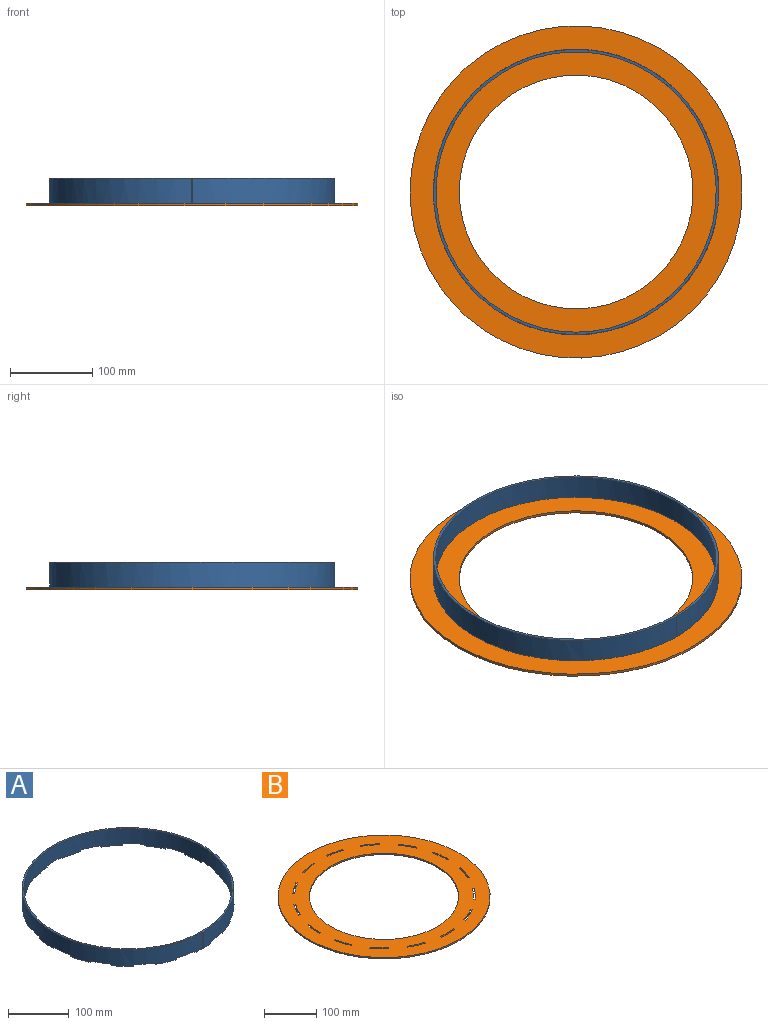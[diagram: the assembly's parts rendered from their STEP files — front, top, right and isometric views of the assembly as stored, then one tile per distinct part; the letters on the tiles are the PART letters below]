
ASSEMBLY  parts=2 mates=1
PART A: 66 faces, bbox 347.8x347.8x33 mm
  f0: plane 3x2.85mm, normal (-0.95,-0.31,0), area 9mm2, adj f1,f63,f64,f65
  f1: plane 34.14x17.39mm, normal (0,0,-1), area 108.3mm2, adj f0,f2,f64,f65
  f2: plane 3x2.6mm, normal (0.87,0.5,0), area 9mm2, adj f1,f3,f64,f65
  f3: plane 30.91x23.6mm, normal (0,0,-1), area 108.3mm2, adj f2,f4,f64,f65
  f4: plane 3x2.23mm, normal (-0.74,-0.67,0), area 9mm2, adj f3,f5,f64,f65
  f5: plane 28.78x26.33mm, normal (0,0,-1), area 108.3mm2, adj f4,f6,f64,f65
  f6: plane 3x2.43mm, normal (0.59,0.81,0), area 9mm2, adj f5,f7,f64,f65
  f7: plane 32.7x20.6mm, normal (0,0,-1), area 108.3mm2, adj f6,f8,f64,f65
  f8: plane 3x2.74mm, normal (-0.41,-0.91,0), area 9mm2, adj f7,f9,f64,f65
  f9: plane 35.2x13.98mm, normal (0,0,-1), area 108.3mm2, adj f8,f10,f64,f65
  f10: plane 3x2.93mm, normal (0.21,0.98,0), area 9mm2, adj f9,f11,f64,f65
  f11: plane 36.16x6.73mm, normal (0,0,-1), area 108.3mm2, adj f10,f12,f64,f65
  f12: plane 3x3mm, normal (0,-1,0), area 9mm2, adj f11,f13,f64,f65
  f13: plane 36.16x6.73mm, normal (0,0,-1), area 108.3mm2, adj f12,f14,f64,f65
  f14: plane 3x2.93mm, normal (-0.21,0.98,0), area 9mm2, adj f13,f15,f64,f65
  f15: plane 35.2x13.98mm, normal (0,0,-1), area 108.3mm2, adj f14,f16,f64,f65
  f16: plane 3x2.74mm, normal (0.41,-0.91,0), area 9mm2, adj f15,f17,f64,f65
  f17: plane 32.7x20.6mm, normal (0,0,-1), area 108.3mm2, adj f16,f18,f64,f65
  f18: plane 3x2.43mm, normal (-0.59,0.81,0), area 9mm2, adj f17,f19,f64,f65
  f19: plane 28.78x26.33mm, normal (0,0,-1), area 108.3mm2, adj f18,f20,f64,f65
  f20: plane 3x2.23mm, normal (0.74,-0.67,0), area 9mm2, adj f19,f21,f64,f65
  f21: plane 30.91x23.6mm, normal (0,0,-1), area 108.3mm2, adj f20,f22,f64,f65
  f22: plane 3x2.6mm, normal (-0.87,0.5,0), area 9mm2, adj f21,f23,f64,f65
  f23: plane 34.14x17.39mm, normal (0,0,-1), area 108.3mm2, adj f22,f24,f64,f65
  f24: plane 3x2.85mm, normal (0.95,-0.31,0), area 9mm2, adj f23,f25,f64,f65
  f25: plane 35.87x10.41mm, normal (0,0,-1), area 108.3mm2, adj f24,f26,f64,f65
  f26: plane 3x2.98mm, normal (-0.99,0.1,0), area 9mm2, adj f25,f27,f64,f65
  f27: plane 18.08x3.94mm, normal (0,0,-1), area 53.9mm2, adj f26,f28,f64,f65
  f28: plane 33x3mm, normal (1,0,0), area 99mm2, adj f27,f29,f64,f65
  f29: plane 347.8x347.8mm, normal (0,0,1), area 3249.1mm2, adj f28,f30,f64,f65
  f30: plane 33x3mm, normal (-1,0,0), area 99mm2, adj f29,f31,f64,f65
  f31: plane 18.08x3.94mm, normal (0,0,-1), area 53.9mm2, adj f30,f32,f64,f65
  f32: plane 3x2.98mm, normal (0.99,0.1,0), area 9mm2, adj f31,f33,f64,f65
  f33: plane 35.87x10.41mm, normal (0,0,-1), area 108.3mm2, adj f32,f34,f64,f65
  f34: plane 3x2.85mm, normal (-0.95,-0.31,0), area 9mm2, adj f33,f35,f64,f65
  f35: plane 34.14x17.39mm, normal (0,0,-1), area 108.3mm2, adj f34,f36,f64,f65
  f36: plane 3x2.6mm, normal (0.87,0.5,0), area 9mm2, adj f35,f37,f64,f65
  f37: plane 30.91x23.6mm, normal (0,0,-1), area 108.3mm2, adj f36,f38,f64,f65
  f38: plane 3x2.23mm, normal (-0.74,-0.67,0), area 9mm2, adj f37,f39,f64,f65
  f39: plane 28.78x26.33mm, normal (0,0,-1), area 108.3mm2, adj f38,f40,f64,f65
  f40: plane 3x2.43mm, normal (0.59,0.81,0), area 9mm2, adj f39,f41,f64,f65
  f41: plane 32.7x20.6mm, normal (0,0,-1), area 108.3mm2, adj f40,f42,f64,f65
  f42: plane 3x2.74mm, normal (-0.41,-0.91,0), area 9mm2, adj f41,f43,f64,f65
  f43: plane 35.2x13.98mm, normal (0,0,-1), area 108.3mm2, adj f42,f44,f64,f65
  f44: plane 3x2.93mm, normal (0.21,0.98,0), area 9mm2, adj f43,f45,f64,f65
  f45: plane 36.16x6.73mm, normal (0,0,-1), area 108.3mm2, adj f44,f46,f64,f65
  f46: plane 3x3mm, normal (0,-1,0), area 9mm2, adj f45,f47,f64,f65
  f47: plane 36.16x6.73mm, normal (0,0,-1), area 108.3mm2, adj f46,f48,f64,f65
  f48: plane 3x2.93mm, normal (-0.21,0.98,0), area 9mm2, adj f47,f49,f64,f65
  f49: plane 35.2x13.98mm, normal (0,0,-1), area 108.3mm2, adj f48,f50,f64,f65
  f50: plane 3x2.74mm, normal (0.41,-0.91,0), area 9mm2, adj f49,f51,f64,f65
  f51: plane 32.7x20.6mm, normal (0,0,-1), area 108.3mm2, adj f50,f52,f64,f65
  f52: plane 3x2.43mm, normal (-0.59,0.81,0), area 9mm2, adj f51,f53,f64,f65
  f53: plane 28.78x26.33mm, normal (0,0,-1), area 108.3mm2, adj f52,f54,f64,f65
  f54: plane 3x2.23mm, normal (0.74,-0.67,0), area 9mm2, adj f53,f55,f64,f65
  f55: plane 30.91x23.6mm, normal (0,0,-1), area 108.3mm2, adj f54,f56,f64,f65
  f56: plane 3x2.6mm, normal (-0.87,0.5,0), area 9mm2, adj f55,f57,f64,f65
  f57: plane 34.14x17.39mm, normal (0,0,-1), area 108.3mm2, adj f56,f58,f64,f65
  f58: plane 3x2.85mm, normal (0.95,-0.31,0), area 9mm2, adj f57,f59,f64,f65
  f59: plane 35.87x10.41mm, normal (0,0,-1), area 108.3mm2, adj f58,f60,f64,f65
  f60: plane 3x2.98mm, normal (-0.99,0.1,0), area 9mm2, adj f59,f61,f64,f65
  f61: plane 36.36x3.94mm, normal (0,0,-1), area 108.3mm2, adj f60,f62,f64,f65
  f62: plane 3x2.98mm, normal (0.99,0.1,0), area 9mm2, adj f61,f63,f64,f65
  f63: plane 35.87x10.41mm, normal (0,0,-1), area 108.3mm2, adj f0,f62,f64,f65
  f64: cylinder r=173.9mm len=347.8mm, axis (0,0,1), area 34411.6mm2, adj f0,f1,f2,f3,f4,f5,f6,f7
  f65: cylinder r=170.9mm len=341.8mm, axis (0,0,1), area 33818mm2, adj f0,f1,f2,f3,f4,f5,f6,f7
PART B: 64 faces, bbox 405x405x3 mm
  f0: plane 3.04x3mm, normal (-0.95,0.31,0), area 9.6mm2, adj f1,f46,f62,f63
  f1: cylinder r=170.9mm len=34.95mm, axis (0,0,-1), area 107.4mm2, adj f0,f2,f62,f63
  f2: plane 3.18x3mm, normal (0.99,-0.1,0), area 9.6mm2, adj f1,f46,f62,f63
  f3: cylinder r=170.9mm len=28.9mm, axis (0,0,-1), area 107.4mm2, adj f4,f47,f62,f63
  f4: plane 3x2.77mm, normal (0.87,-0.5,0), area 9.6mm2, adj f3,f5,f62,f63
  f5: cylinder r=174.1mm len=29.45mm, axis (0,0,-1), area 109.4mm2, adj f4,f47,f62,f63
  f6: cylinder r=170.9mm len=30.94mm, axis (0,0,-1), area 107.4mm2, adj f7,f48,f62,f63
  f7: plane 3x2.59mm, normal (0.59,-0.81,0), area 9.6mm2, adj f6,f8,f62,f63
  f8: cylinder r=174.1mm len=31.52mm, axis (0,0,-1), area 109.4mm2, adj f7,f48,f62,f63
  f9: cylinder r=170.9mm len=35.53mm, axis (0,0,-1), area 107.4mm2, adj f10,f49,f62,f63
  f10: plane 3.13x3mm, normal (0.21,-0.98,0), area 9.6mm2, adj f9,f11,f62,f63
  f11: cylinder r=174.1mm len=36.2mm, axis (0,0,-1), area 109.4mm2, adj f10,f49,f62,f63
  f12: cylinder r=170.9mm len=33.98mm, axis (0,0,-1), area 107.4mm2, adj f13,f50,f62,f63
  f13: plane 3.13x3mm, normal (-0.21,-0.98,0), area 9.6mm2, adj f12,f14,f62,f63
  f14: cylinder r=174.1mm len=34.62mm, axis (0,0,-1), area 109.4mm2, adj f13,f50,f62,f63
  f15: cylinder r=170.9mm len=26.55mm, axis (0,0,-1), area 107.4mm2, adj f16,f51,f62,f63
  f16: plane 3x2.59mm, normal (-0.59,-0.81,0), area 9.6mm2, adj f15,f17,f62,f63
  f17: cylinder r=174.1mm len=27.05mm, axis (0,0,-1), area 109.4mm2, adj f16,f51,f62,f63
  f18: cylinder r=170.9mm len=32.64mm, axis (0,0,-1), area 107.4mm2, adj f19,f52,f62,f63
  f19: plane 3x2.77mm, normal (-0.87,-0.5,0), area 9.6mm2, adj f18,f20,f62,f63
  f20: cylinder r=174.1mm len=33.25mm, axis (0,0,-1), area 109.4mm2, adj f19,f52,f62,f63
  f21: cylinder r=170.9mm len=35.73mm, axis (0,0,-1), area 107.4mm2, adj f22,f53,f62,f63
  f22: plane 3.18x3mm, normal (-0.99,-0.1,0), area 9.6mm2, adj f21,f23,f62,f63
  f23: cylinder r=174.1mm len=36.4mm, axis (0,0,-1), area 109.4mm2, adj f22,f53,f62,f63
  f24: cylinder r=170.9mm len=32.64mm, axis (0,0,-1), area 107.4mm2, adj f25,f54,f62,f63
  f25: plane 3.04x3mm, normal (-0.95,0.31,0), area 9.6mm2, adj f24,f26,f62,f63
  f26: cylinder r=174.1mm len=33.25mm, axis (0,0,-1), area 109.4mm2, adj f25,f54,f62,f63
  f27: cylinder r=170.9mm len=26.55mm, axis (0,0,-1), area 107.4mm2, adj f28,f55,f62,f63
  f28: plane 3x2.38mm, normal (-0.74,0.67,0), area 9.6mm2, adj f27,f29,f62,f63
  f29: cylinder r=174.1mm len=27.05mm, axis (0,0,-1), area 109.4mm2, adj f28,f55,f62,f63
  f30: cylinder r=170.9mm len=33.98mm, axis (0,0,-1), area 107.4mm2, adj f31,f56,f62,f63
  f31: plane 3x2.92mm, normal (-0.41,0.91,0), area 9.6mm2, adj f30,f32,f62,f63
  f32: cylinder r=174.1mm len=34.62mm, axis (0,0,-1), area 109.4mm2, adj f31,f56,f62,f63
  f33: cylinder r=170.9mm len=35.53mm, axis (0,0,-1), area 107.4mm2, adj f34,f57,f62,f63
  f34: plane 3.2x3mm, normal (0,1,0), area 9.6mm2, adj f33,f35,f62,f63
  f35: cylinder r=174.1mm len=36.2mm, axis (0,0,-1), area 109.4mm2, adj f34,f57,f62,f63
  f36: cylinder r=170.9mm len=30.94mm, axis (0,0,-1), area 107.4mm2, adj f37,f58,f62,f63
  f37: plane 3x2.92mm, normal (0.41,0.91,0), area 9.6mm2, adj f36,f38,f62,f63
  f38: cylinder r=174.1mm len=31.52mm, axis (0,0,-1), area 109.4mm2, adj f37,f58,f62,f63
  f39: cylinder r=170.9mm len=28.9mm, axis (0,0,-1), area 107.4mm2, adj f40,f59,f62,f63
  f40: plane 3x2.38mm, normal (0.74,0.67,0), area 9.6mm2, adj f39,f41,f62,f63
  f41: cylinder r=174.1mm len=29.45mm, axis (0,0,-1), area 109.4mm2, adj f40,f59,f62,f63
  f42: cylinder r=170.9mm len=34.95mm, axis (0,0,-1), area 107.4mm2, adj f43,f60,f62,f63
  f43: plane 3.04x3mm, normal (0.95,0.31,0), area 9.6mm2, adj f42,f44,f62,f63
  f44: cylinder r=174.1mm len=35.6mm, axis (0,0,-1), area 109.4mm2, adj f43,f60,f62,f63
  f45: cylinder r=142.5mm len=285mm, axis (0,0,-1), area 2686.1mm2, adj f62,f63
  f46: cylinder r=174.1mm len=35.6mm, axis (0,0,-1), area 109.4mm2, adj f0,f2,f62,f63
  f47: plane 3x2.38mm, normal (-0.74,0.67,0), area 9.6mm2, adj f3,f5,f62,f63
  f48: plane 3x2.92mm, normal (-0.41,0.91,0), area 9.6mm2, adj f6,f8,f62,f63
  f49: plane 3.2x3mm, normal (0,1,0), area 9.6mm2, adj f9,f11,f62,f63
  f50: plane 3x2.92mm, normal (0.41,0.91,0), area 9.6mm2, adj f12,f14,f62,f63
  f51: plane 3x2.38mm, normal (0.74,0.67,0), area 9.6mm2, adj f15,f17,f62,f63
  f52: plane 3.04x3mm, normal (0.95,0.31,0), area 9.6mm2, adj f18,f20,f62,f63
  f53: plane 3.18x3mm, normal (0.99,-0.1,0), area 9.6mm2, adj f21,f23,f62,f63
  f54: plane 3x2.77mm, normal (0.87,-0.5,0), area 9.6mm2, adj f24,f26,f62,f63
  f55: plane 3x2.59mm, normal (0.59,-0.81,0), area 9.6mm2, adj f27,f29,f62,f63
  f56: plane 3.13x3mm, normal (0.21,-0.98,0), area 9.6mm2, adj f30,f32,f62,f63
  f57: plane 3.13x3mm, normal (-0.21,-0.98,0), area 9.6mm2, adj f33,f35,f62,f63
  f58: plane 3x2.59mm, normal (-0.59,-0.81,0), area 9.6mm2, adj f36,f38,f62,f63
  f59: plane 3x2.77mm, normal (-0.87,-0.5,0), area 9.6mm2, adj f39,f41,f62,f63
  f60: plane 3.18x3mm, normal (-0.99,-0.1,0), area 9.6mm2, adj f42,f44,f62,f63
  f61: cylinder r=202.5mm len=405mm, axis (0,0,-1), area 3817mm2, adj f62,f63
  f62: plane 405x405mm, normal (0,0,1), area 63296.8mm2, adj f0,f1,f2,f3,f4,f5,f6,f7
  f63: plane 405x405mm, normal (0,0,-1), area 63296.8mm2, adj f0,f1,f2,f3,f4,f5,f6,f7
PLACE A t=(65.14,39.76,51.77)mm
PLACE B rot(axis=(0.87,0.5,0),180deg) t=(74.4,34.47,54.77)mm
MATE fastened B.f28 <-> A.f14  axis (0.21,-0.98,0) through (-103.49,3.92,53.27)mm
